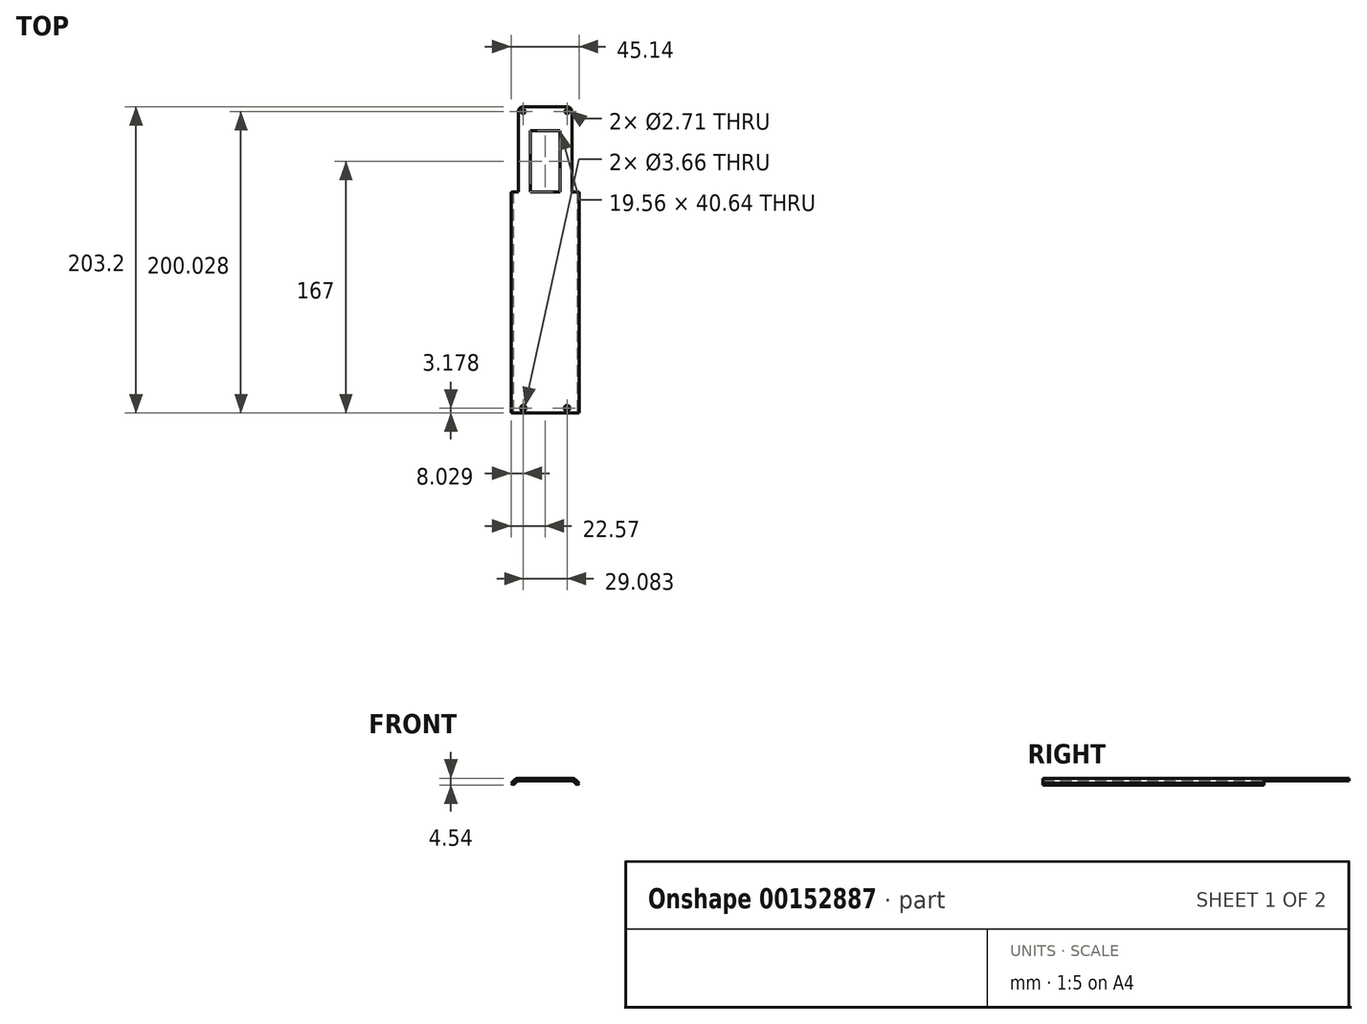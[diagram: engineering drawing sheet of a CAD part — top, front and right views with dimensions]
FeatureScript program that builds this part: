
annotation { "Feature Type Name" : "Feature", "Feature Type Description" : "" }
export const myFeature = defineFeature(function(context is Context, id is Id, definition is map)
    precondition{}
    {
        {
            var Q0;
            Q0=qCreatedBy(makeId("Top.planeOp"),FACE);
            var sketch = newSketch(context, id + "F0", { "sketchPlane" : qUnion([Q0])});
            skLineSegment(sketch, "E0.bottom", {"start": v(9.78, -20.32) * mm, "end": v(-9.78, -20.32) * mm});
            skLineSegment(sketch, "E0.top", {"start": v(9.78, 20.32) * mm, "end": v(-9.78, 20.32) * mm});
            skLineSegment(sketch, "E0.left", {"start": v(9.78, -20.32) * mm, "end": v(9.78, 20.32) * mm});
            skLineSegment(sketch, "E0.right", {"start": v(-9.78, -20.32) * mm, "end": v(-9.78, 20.32) * mm});
            skPoint(sketch, "E0.middle", {"position": v(0, 0) * mm});
            skLineSegment(sketch, "E1", {"start": v(-17.72, 36.2) * mm, "end": v(17.72, 36.2) * mm});
            skLineSegment(sketch, "E2", {"start": v(-17.72, 36.2) * mm, "end": v(-17.72, -167) * mm});
            skLineSegment(sketch, "E3", {"start": v(-17.72, -167) * mm, "end": v(17.72, -167) * mm});
            skLineSegment(sketch, "E4", {"start": v(17.72, -167) * mm, "end": v(17.72, 36.2) * mm});
            skLineSegment(sketch, "E5", {"start": v(0, -167) * mm, "end": v(0, -163.82) * mm, "construction": true});
            skLineSegment(sketch, "E6", {"start": v(14.54, -163.82) * mm, "end": v(-14.54, -163.82) * mm, "construction": true});
            skLineSegment(sketch, "E7", {"start": v(-14.54, -163.82) * mm, "end": v(-17.72, -163.82) * mm, "construction": true});
            skCircle(sketch, "E8", {"center": v(-14.54, -163.82) * mm, "radius": 1.83 * mm});
            skCircle(sketch, "E9", {"center": v(14.54, -163.82) * mm, "radius": 1.83 * mm});
            skLineSegment(sketch, "E10", {"start": v(-14.54, 33.03) * mm, "end": v(14.54, 33.03) * mm, "construction": true});
            skCircle(sketch, "E11", {"center": v(-14.54, 33.03) * mm, "radius": 1.35 * mm});
            skCircle(sketch, "E12", {"center": v(14.54, 33.03) * mm, "radius": 1.35 * mm});
            skLineSegment(sketch, "E13", {"start": v(0, 33.03) * mm, "end": v(0, 36.2) * mm, "construction": true});
            skLineSegment(sketch, "E14", {"start": v(14.54, 33.03) * mm, "end": v(17.72, 33.03) * mm, "construction": true});
            skLineSegment(sketch, "E15", {"start": v(0, 20.32) * mm, "end": v(0, 10.9) * mm, "construction": true});
            skLineSegment(sketch, "E16", {"start": v(0, 20.32) * mm, "end": v(0, 33.03) * mm, "construction": true});
            skSolve(sketch);
        }
        {
            var Q0;
            Q0=qSketchRegion(id+"F0",true);
            extrude(context, id + "F1", {"entities" : qUnion([Q0]), "depth" : 1.7 * mm});
        }
        {
            var Q0;
            Q0=makeQuery(id+"F1.opExtrude","SWEPT_FACE",FACE,{"disambiguationData":[OSD([sQuery(id+"F0.wireOp",EDGE,"E3")])]});
            var sketch = newSketch(context, id + "F2", { "sketchPlane" : qUnion([Q0])});
            skArc(sketch, "E17", {"start": v(-17.72, 0) * mm, "mid": v(-18.48, -0.15) * mm, "end": v(-19.12, -0.58) * mm});
            skArc(sketch, "E18", {"start": v(-17.72, 1.7) * mm, "mid": v(-19.13, 1.43) * mm, "end": v(-20.33, 0.63) * mm});
            skArc(sketch, "E19", {"start": v(19.12, -0.58) * mm, "mid": v(18.48, -0.15) * mm, "end": v(17.72, 0) * mm});
            skArc(sketch, "E20", {"start": v(20.33, 0.63) * mm, "mid": v(19.13, 1.43) * mm, "end": v(17.72, 1.7) * mm});
            skLineSegment(sketch, "E21.bottom", {"start": v(-20.33, 0.63) * mm, "end": v(-22.57, -1.62) * mm});
            skLineSegment(sketch, "E21.top", {"start": v(-19.12, -0.58) * mm, "end": v(-21.36, -2.83) * mm});
            skLineSegment(sketch, "E21.left", {"start": v(-20.33, 0.63) * mm, "end": v(-19.12, -0.58) * mm, "construction": true});
            skLineSegment(sketch, "E21.right", {"start": v(-22.57, -1.62) * mm, "end": v(-21.36, -2.83) * mm});
            skLineSegment(sketch, "E22", {"start": v(-17.72, 1.7) * mm, "end": v(-17.72, 0) * mm});
            skLineSegment(sketch, "E23.bottom", {"start": v(20.33, 0.63) * mm, "end": v(22.57, -1.62) * mm});
            skLineSegment(sketch, "E23.top", {"start": v(19.12, -0.58) * mm, "end": v(21.36, -2.83) * mm});
            skLineSegment(sketch, "E23.left", {"start": v(20.33, 0.63) * mm, "end": v(19.12, -0.58) * mm, "construction": true});
            skLineSegment(sketch, "E23.right", {"start": v(22.57, -1.62) * mm, "end": v(21.36, -2.83) * mm});
            skLineSegment(sketch, "E24", {"start": v(19.12, -0.58) * mm, "end": v(-19.12, -0.58) * mm, "construction": true});
            skLineSegment(sketch, "E25", {"start": v(0, 0) * mm, "end": v(0, -0.58) * mm, "construction": true});
            skSolve(sketch);
        }
        {
            var Q0;
            Q0=qSketchRegion(id+"F2",true);
            var Q1;
            Q1=makeQuery(id+"F2.imprint","IMPRINT",FACE,{"disambiguationData":[TD([[makeQuery(id+"F2.imprint","IMPRINT",EDGE,{"derivedFrom":sQuery(id+"F2.wireOp",EDGE,"E19")}),-1.0]])]});
            var Q2;
            Q2=makeQuery(id+"F1.opExtrude","SWEPT_FACE",FACE,{"disambiguationData":[OSD([sQuery(id+"F0.wireOp",EDGE,"E0.bottom")])]});
            extrude(context, id + "F3", {"entities" : qUnion([Q0, Q1]), "operationType" : NewBodyOperationType.ADD, "endBound" : BoundingType.UP_TO_SURFACE, "oppositeDirection" : true, "endBoundEntityFace" : qUnion([Q2]), "depth" : 25.4 * mm});
        }
        {
            var Q0;
            Q0=makeQuery(id+"F1.opExtrude","SWEPT_EDGE",EDGE,{"disambiguationData":[OSD([sQuery(id+"F0.wireOp",EDGE,"E1"),sQuery(id+"F0.wireOp",EDGE,"E4")])]});
            var Q1;
            Q1=makeQuery(id+"F1.opExtrude","SWEPT_EDGE",EDGE,{"disambiguationData":[OSD([sQuery(id+"F0.wireOp",EDGE,"E1"),sQuery(id+"F0.wireOp",EDGE,"E2")])]});
            fillet(context, id + "F4", {"entities" : qUnion([Q0, Q1]), "radius" : 3.17 * mm, "allowEdgeOverflow" : false});
        }
    });
